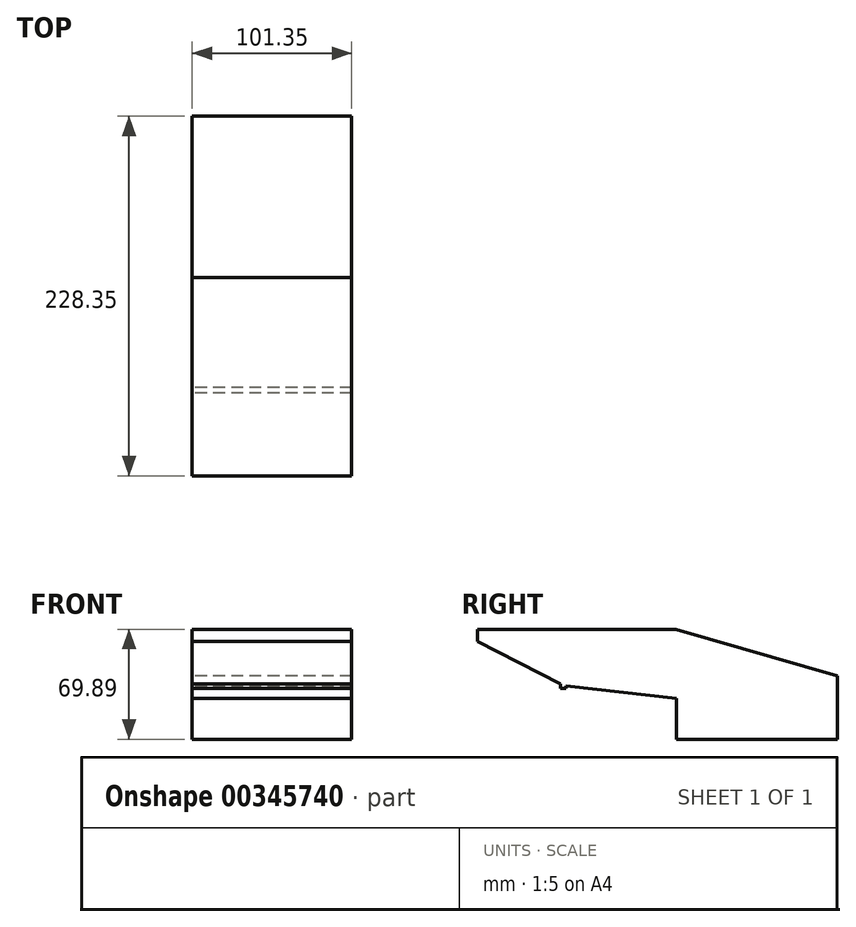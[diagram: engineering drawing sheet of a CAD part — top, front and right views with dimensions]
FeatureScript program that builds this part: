
annotation { "Feature Type Name" : "Feature", "Feature Type Description" : "" }
export const myFeature = defineFeature(function(context is Context, id is Id, definition is map)
    precondition{}
    {
        {
            var Q0;
            Q0=qCreatedBy(makeId("Right.planeOp"),FACE);
            var sketch = newSketch(context, id + "F0", { "sketchPlane" : qUnion([Q0])});
            skLineSegment(sketch, "E0.bottom", {"start": v(-56.03, 0) * mm, "end": v(69.85, 0) * mm});
            skLineSegment(sketch, "E0.top", {"start": v(-56.03, 7.89) * mm, "end": v(69.85, 7.89) * mm});
            skLineSegment(sketch, "E0.left", {"start": v(-56.03, 0) * mm, "end": v(-56.03, 7.89) * mm});
            skLineSegment(sketch, "E0.right", {"start": v(69.85, 0) * mm, "end": v(69.85, 7.89) * mm});
            skPoint(sketch, "E0.middle", {"position": v(6.9, 3.94) * mm});
            skLineSegment(sketch, "E1.bottom", {"start": v(70.34, -21.91) * mm, "end": v(172.32, -21.91) * mm});
            skLineSegment(sketch, "E1.top", {"start": v(70.34, -62) * mm, "end": v(172.32, -62) * mm});
            skLineSegment(sketch, "E1.left", {"start": v(70.34, -21.91) * mm, "end": v(70.34, -62) * mm});
            skLineSegment(sketch, "E1.right", {"start": v(172.32, -21.91) * mm, "end": v(172.32, -62) * mm});
            skPoint(sketch, "E1.middle", {"position": v(121.33, -41.96) * mm});
            skLineSegment(sketch, "E2.bottom", {"start": v(0, -25.97) * mm, "end": v(-3.56, -25.97) * mm});
            skLineSegment(sketch, "E2.top", {"start": v(0, -29.72) * mm, "end": v(-3.56, -29.72) * mm});
            skLineSegment(sketch, "E2.left", {"start": v(0, -25.97) * mm, "end": v(0, -29.72) * mm});
            skLineSegment(sketch, "E2.right", {"start": v(-3.56, -25.97) * mm, "end": v(-3.56, -29.72) * mm});
            skPoint(sketch, "E2.middle", {"position": v(-1.78, -27.84) * mm});
            skLineSegment(sketch, "E3", {"start": v(121.33, -41.96) * mm, "end": v(-1.78, -27.84) * mm});
            skLineSegment(sketch, "E4", {"start": v(1.74, -12.85) * mm, "end": v(6.9, 3.94) * mm});
            skLineSegment(sketch, "E5", {"start": v(69.85, 0) * mm, "end": v(70.34, -21.91) * mm});
            skLineSegment(sketch, "E6", {"start": v(-1.78, -27.84) * mm, "end": v(-56.03, 0) * mm});
            skLineSegment(sketch, "E7", {"start": v(69.85, 0) * mm, "end": v(172.32, -21.91) * mm});
            skLineSegment(sketch, "E8", {"start": v(69.85, 7.89) * mm, "end": v(172.32, -21.91) * mm});
            skSolve(sketch);
        }
        {
            var Q0;
            Q0 = qSketchRegion(id + "F0", true);
            extrude(context, id + "F1", {"entities" : qUnion([Q0]), "depth" : 101.35 * mm});
        }
    });
